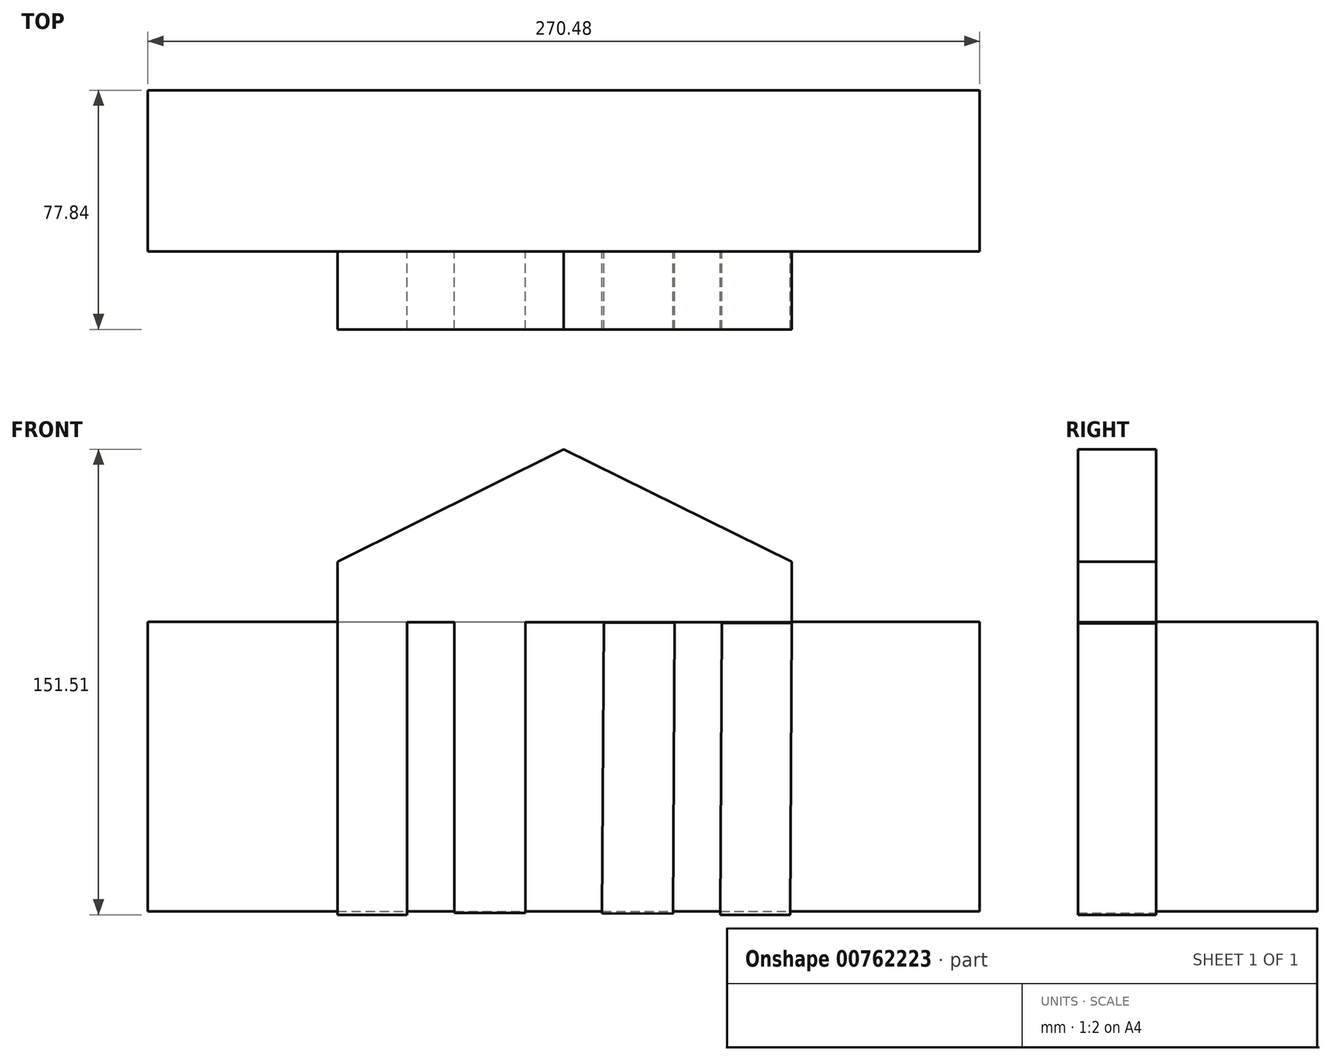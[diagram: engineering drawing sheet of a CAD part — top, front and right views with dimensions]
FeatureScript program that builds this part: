
annotation { "Feature Type Name" : "Feature", "Feature Type Description" : "" }
export const myFeature = defineFeature(function(context is Context, id is Id, definition is map)
    precondition{}
    {
        {
            var Q0;
            Q0=qCreatedBy(makeId("Front.planeOp"),FACE);
            var sketch = newSketch(context, id + "F0", { "sketchPlane" : qUnion([Q0])});
            skLineSegment(sketch, "E0.bottom", {"start": v(-73.6, 19.68) * mm, "end": v(-50.9, 19.68) * mm});
            skLineSegment(sketch, "E0.top", {"start": v(-73.6, -75.89) * mm, "end": v(-50.9, -75.89) * mm});
            skLineSegment(sketch, "E0.left", {"start": v(-73.6, 19.68) * mm, "end": v(-73.6, -75.89) * mm});
            skLineSegment(sketch, "E0.right", {"start": v(-50.9, 19.68) * mm, "end": v(-50.9, -75.89) * mm});
            skLineSegment(sketch, "E1.bottom", {"start": v(-73.6, 19.68) * mm, "end": v(74.14, 19.68) * mm});
            skLineSegment(sketch, "E1.top", {"start": v(-73.6, 39.4) * mm, "end": v(74.14, 39.4) * mm});
            skLineSegment(sketch, "E1.left", {"start": v(-73.6, 19.68) * mm, "end": v(-73.6, 39.4) * mm});
            skLineSegment(sketch, "E1.right", {"start": v(74.14, 19.68) * mm, "end": v(74.14, 39.4) * mm});
            skLineSegment(sketch, "E2.bottom", {"start": v(-35.57, 19.68) * mm, "end": v(-12.5, 19.68) * mm});
            skLineSegment(sketch, "E2.top", {"start": v(-35.57, -74.97) * mm, "end": v(-12.5, -74.97) * mm});
            skLineSegment(sketch, "E2.left", {"start": v(-35.57, 19.68) * mm, "end": v(-35.57, -74.97) * mm});
            skLineSegment(sketch, "E2.right", {"start": v(-12.5, 19.68) * mm, "end": v(-12.5, -74.97) * mm});
            skLineSegment(sketch, "E3.MirrorCS", {"start": v(13.04, 19.61) * mm, "end": v(12.5, -75.04) * mm});
            skLineSegment(sketch, "E4.MirrorCS", {"start": v(36.11, 19.48) * mm, "end": v(35.58, -75.17) * mm});
            skLineSegment(sketch, "E5.MirrorCS", {"start": v(74.14, 19.26) * mm, "end": v(-73.6, 20.1) * mm});
            skLineSegment(sketch, "E6.MirrorCS", {"start": v(35.58, -75.17) * mm, "end": v(12.5, -75.04) * mm});
            skLineSegment(sketch, "E7.MirrorCS", {"start": v(73.6, -76.3) * mm, "end": v(50.9, -76.17) * mm});
            skLineSegment(sketch, "E8.MirrorCS", {"start": v(74.14, 19.26) * mm, "end": v(73.6, -76.3) * mm});
            skLineSegment(sketch, "E9.MirrorCS", {"start": v(51.44, 19.4) * mm, "end": v(50.9, -76.17) * mm});
            skPoint(sketch, "E10.end.orphan", {"position": v(0, -76) * mm});
            skPoint(sketch, "E10.start.orphan", {"position": v(0.27, 19.68) * mm});
            skLineSegment(sketch, "E11", {"start": v(-73.6, 39.4) * mm, "end": v(0, 75.99) * mm});
            skLineSegment(sketch, "E12", {"start": v(0, 75.99) * mm, "end": v(74.14, 39.4) * mm});
            skLineSegment(sketch, "E13.bottom", {"start": v(0.27, 19.68) * mm, "end": v(142.07, 19.68) * mm});
            skLineSegment(sketch, "E13.top", {"start": v(0.27, -75.52) * mm, "end": v(142.07, -75.52) * mm});
            skLineSegment(sketch, "E13.left", {"start": v(0.27, 19.68) * mm, "end": v(0.27, -75.52) * mm});
            skLineSegment(sketch, "E13.right", {"start": v(142.07, 19.68) * mm, "end": v(142.07, -75.52) * mm});
            skLineSegment(sketch, "E14.MirrorCS", {"start": v(0.27, 19.68) * mm, "end": v(-141.52, 19.68) * mm});
            skLineSegment(sketch, "E15.MirrorCS", {"start": v(0.27, -75.52) * mm, "end": v(-141.52, -75.52) * mm});
            skLineSegment(sketch, "E16.MirrorCS", {"start": v(-141.52, 19.68) * mm, "end": v(-141.52, -75.52) * mm});
            skSolve(sketch);
        }
        {
            var Q0;
            {var subQ0=sQuery(id+"F0.wireOp",EDGE,"E0.bottom");Q0=makeQuery(id+"F0.imprint","IMPRINT",FACE,{"disambiguationData":[TD([[makeQuery(id+"F0.imprint","IMPRINT",EDGE,{"derivedFrom":subQ0}),-1.0]])]});}
            var Q1;
            Q1=makeQuery(id+"F0.imprint","IMPRINT",FACE,{"disambiguationData":[TD([[makeQuery(id+"F0.imprint","IMPRINT",EDGE,{"derivedFrom":sQuery(id+"F0.wireOp",EDGE,"E2.top")}),1.0]])]});
            var Q2;
            {var subQ0=sQuery(id+"F0.wireOp",EDGE,"E3.MirrorCS");Q2=makeQuery(id+"F0.imprint","IMPRINT",FACE,{"disambiguationData":[TD([[makeQuery(id+"F0.imprint","IMPRINT",EDGE,{"derivedFrom":subQ0}),1.0]])]});}
            var Q3;
            {var subQ0=sQuery(id+"F0.wireOp",EDGE,"E8.MirrorCS");var subQ1=sQuery(id+"F0.wireOp",EDGE,"E5.MirrorCS");var subQ2=makeQuery(id+"F0.imprint","INTERSECT",VERTEX,{"derivedFrom":[subQ1,subQ0]});Q3=makeQuery(id+"F0.imprint","IMPRINT",FACE,{"disambiguationData":[TD([[makeQuery(id+"F0.imprint","IMPRINT",EDGE,{"disambiguationData":[TD([[subQ2,-1.0]])],"derivedFrom":subQ1}),1.0]])]});}
            var Q4;
            {var subQ1=sQuery(id+"F0.wireOp",EDGE,"E0.bottom");Q4=makeQuery(id+"F0.imprint","IMPRINT",FACE,{"disambiguationData":[TD([[makeQuery(id+"F0.imprint","IMPRINT",EDGE,{"derivedFrom":subQ1}),1.0]])]});}
            var Q5;
            Q5=makeQuery(id+"F0.imprint","IMPRINT",FACE,{"disambiguationData":[TD([[makeQuery(id+"F0.imprint","IMPRINT",EDGE,{"derivedFrom":sQuery(id+"F0.wireOp",EDGE,"E1.top")}),1.0]])]});
            extrude(context, id + "F1", {"entities" : qUnion([Q0, Q1, Q2, Q3, Q4, Q5]), "depth" : 25.4 * mm, "offsetDistance" : 25.4 * mm});
        }
        {
            var Q0;
            Q0=qCreatedBy(makeId("Front.planeOp"),FACE);
            var sketch = newSketch(context, id + "F2", { "sketchPlane" : qUnion([Q0])});
            skLineSegment(sketch, "E17.bottom", {"start": v(0, 19.85) * mm, "end": v(135.24, 19.85) * mm});
            skLineSegment(sketch, "E17.top", {"start": v(0, -74.45) * mm, "end": v(135.24, -74.45) * mm});
            skLineSegment(sketch, "E17.left", {"start": v(0, 19.85) * mm, "end": v(0, -74.45) * mm});
            skLineSegment(sketch, "E17.right", {"start": v(135.24, 19.85) * mm, "end": v(135.24, -74.45) * mm});
            skLineSegment(sketch, "E18.MirrorCS", {"start": v(0, 19.85) * mm, "end": v(-135.24, 19.85) * mm});
            skLineSegment(sketch, "E19.MirrorCS", {"start": v(0, -74.45) * mm, "end": v(-135.24, -74.45) * mm});
            skLineSegment(sketch, "E20", {"start": v(-135.24, 19.85) * mm, "end": v(-135.24, -74.45) * mm});
            skSolve(sketch);
        }
        {
            var Q0;
            Q0 = qSketchRegion(id + "F2", true);
            extrude(context, id + "F3", {"entities" : qUnion([Q0]), "oppositeDirection" : true, "depth" : 52.44 * mm, "offsetDistance" : 25.4 * mm});
        }
    });
